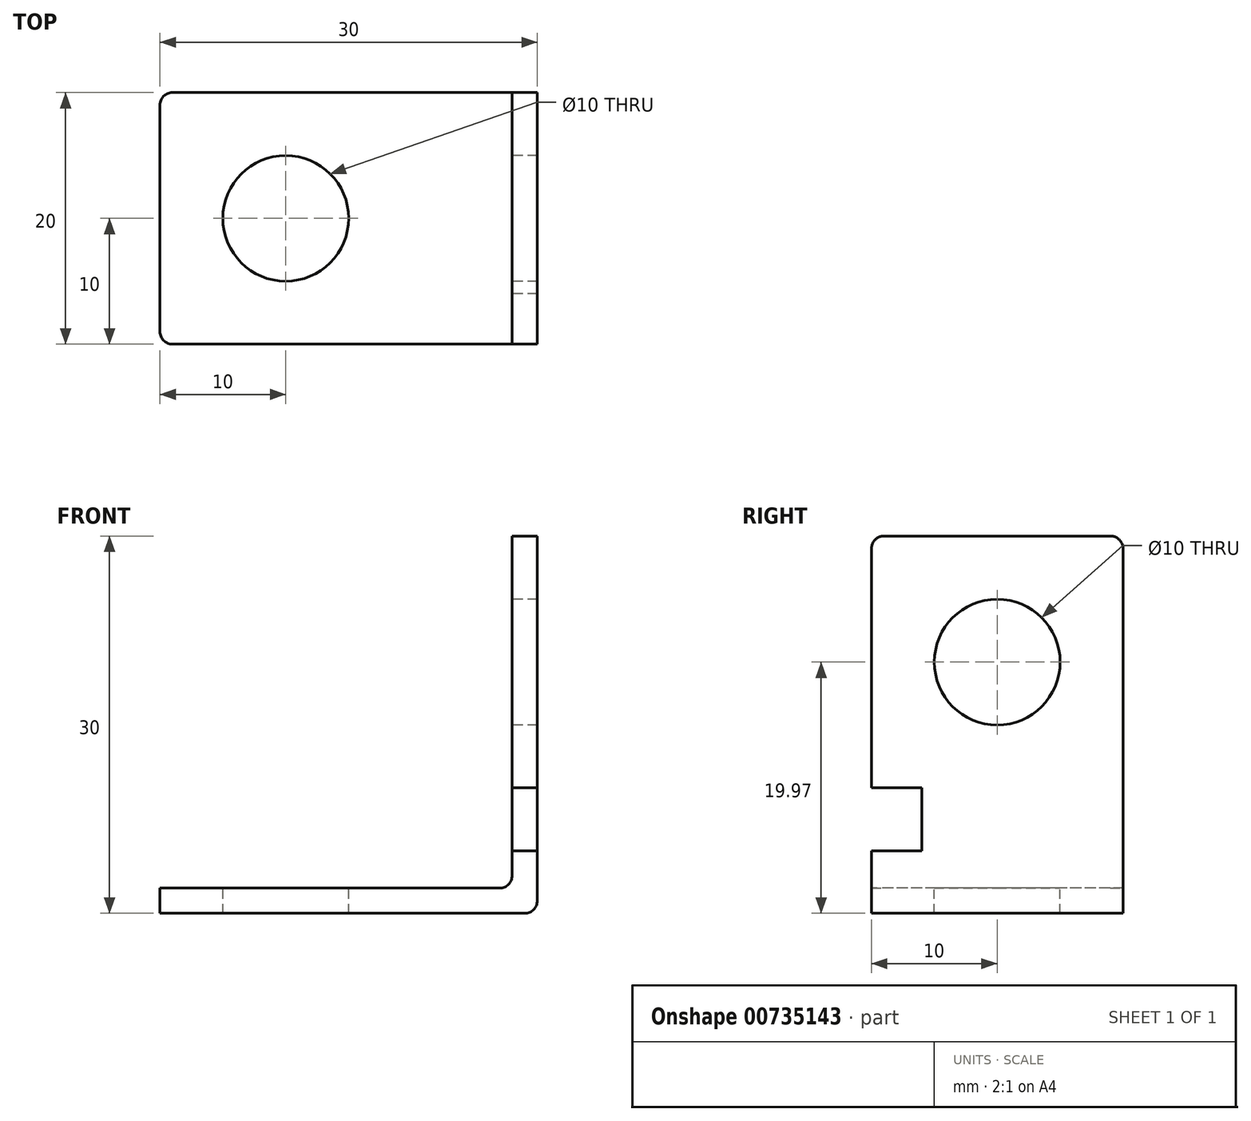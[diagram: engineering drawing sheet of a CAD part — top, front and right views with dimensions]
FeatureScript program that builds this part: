
annotation { "Feature Type Name" : "Feature", "Feature Type Description" : "" }
export const myFeature = defineFeature(function(context is Context, id is Id, definition is map)
    precondition{}
    {
        {
            var Q0;
            Q0=qCreatedBy(makeId("Front.planeOp"),FACE);
            var sketch = newSketch(context, id + "F0", { "sketchPlane" : qUnion([Q0])});
            skLineSegment(sketch, "E0", {"start": v(0, 0) * mm, "end": v(29, 0) * mm});
            skLineSegment(sketch, "E1", {"start": v(0, 0) * mm, "end": v(0, 2) * mm});
            skLineSegment(sketch, "E2", {"start": v(0, 2) * mm, "end": v(27, 2) * mm});
            skLineSegment(sketch, "E3", {"start": v(28, 3) * mm, "end": v(28, 29.97) * mm});
            skLineSegment(sketch, "E4", {"start": v(30, 1) * mm, "end": v(30, 30) * mm});
            skLineSegment(sketch, "E5", {"start": v(28, 29.97) * mm, "end": v(30, 30) * mm});
            skPoint(sketch, "E6.visualSharp", {"position": v(28, 2) * mm});
            skArc(sketch, "E6.filletArc", {"start": v(27, 2) * mm, "mid": v(27.7, 2.3) * mm, "end": v(28, 3) * mm});
            skPoint(sketch, "E7.visualSharp", {"position": v(30, 0) * mm});
            skArc(sketch, "E7.filletArc", {"start": v(29, 0) * mm, "mid": v(29.7, 0.3) * mm, "end": v(30, 1) * mm});
            skSolve(sketch);
        }
        {
            var Q0;
            Q0 = qSketchRegion(id + "F0", true);
            extrude(context, id + "F1", {"entities" : qUnion([Q0]), "oppositeDirection" : true, "depth" : 20 * mm, "offsetDistance" : 25 * mm});
        }
        {
            var Q0;
            Q0=makeQuery(id+"F1.opExtrude","SWEPT_FACE",FACE,{"disambiguationData":[OSD([sQuery(id+"F0.wireOp",EDGE,"E2")])]});
            var sketch = newSketch(context, id + "F2", { "sketchPlane" : qUnion([Q0])});
            skCircle(sketch, "E8", {"center": v(10, 10) * mm, "radius": 5 * mm});
            skSolve(sketch);
        }
        {
            var Q0;
            Q0 = qSketchRegion(id + "F2", true);
            extrude(context, id + "F3", {"entities" : qUnion([Q0]), "operationType" : NewBodyOperationType.REMOVE, "endBound" : BoundingType.THROUGH_ALL, "oppositeDirection" : true, "depth" : 25 * mm, "offsetDistance" : 25 * mm});
        }
        {
            var Q0;
            Q0=makeQuery(id+"F1.opExtrude","SWEPT_FACE",FACE,{"disambiguationData":[OSD([sQuery(id+"F0.wireOp",EDGE,"E3")])]});
            var sketch = newSketch(context, id + "F4", { "sketchPlane" : qUnion([Q0])});
            skCircle(sketch, "E9", {"center": v(-10, 19.97) * mm, "radius": 5 * mm});
            skSolve(sketch);
        }
        {
            var Q0;
            Q0 = qSketchRegion(id + "F4", true);
            extrude(context, id + "F5", {"entities" : qUnion([Q0]), "operationType" : NewBodyOperationType.REMOVE, "endBound" : BoundingType.THROUGH_ALL, "oppositeDirection" : true, "depth" : 25 * mm, "offsetDistance" : 25 * mm});
        }
        {
            var Q0;
            Q0=makeQuery(id+"F1.opExtrude","SWEPT_FACE",FACE,{"disambiguationData":[OSD([sQuery(id+"F0.wireOp",EDGE,"E3")])]});
            var sketch = newSketch(context, id + "F6", { "sketchPlane" : qUnion([Q0])});
            skLineSegment(sketch, "E10", {"start": v(0, 9.97) * mm, "end": v(-4, 9.97) * mm});
            skLineSegment(sketch, "E11", {"start": v(-4, 9.97) * mm, "end": v(-4, 4.97) * mm});
            skLineSegment(sketch, "E12", {"start": v(-4, 4.97) * mm, "end": v(0, 4.97) * mm});
            skLineSegment(sketch, "E13", {"start": v(0, 4.97) * mm, "end": v(0, 9.97) * mm});
            skSolve(sketch);
        }
        {
            var Q0;
            Q0 = qSketchRegion(id + "F6", true);
            extrude(context, id + "F7", {"entities" : qUnion([Q0]), "operationType" : NewBodyOperationType.REMOVE, "endBound" : BoundingType.THROUGH_ALL, "oppositeDirection" : true, "depth" : 25 * mm, "offsetDistance" : 25 * mm});
        }
        {
            var Q0;
            Q0=makeQuery(id+"F1.opExtrude","CAP_EDGE",EDGE,{"disambiguationData":[OSD([sQuery(id+"F0.wireOp",EDGE,"E1")])],"isStart":true});
            var Q1;
            Q1=makeQuery(id+"F1.opExtrude","CAP_EDGE",EDGE,{"disambiguationData":[OSD([sQuery(id+"F0.wireOp",EDGE,"E5")])],"isStart":true});
            var Q2;
            Q2=makeQuery(id+"F1.opExtrude","CAP_EDGE",EDGE,{"disambiguationData":[OSD([sQuery(id+"F0.wireOp",EDGE,"E1")])],"isStart":false});
            var Q3;
            Q3=makeQuery(id+"F1.opExtrude","CAP_EDGE",EDGE,{"disambiguationData":[OSD([sQuery(id+"F0.wireOp",EDGE,"E5")])],"isStart":false});
            fillet(context, id + "F8", {"entities" : qUnion([Q0, Q1, Q2, Q3]), "radius" : 1 * mm, "tangentPropagation" : true, "allowEdgeOverflow" : false});
        }
    });
